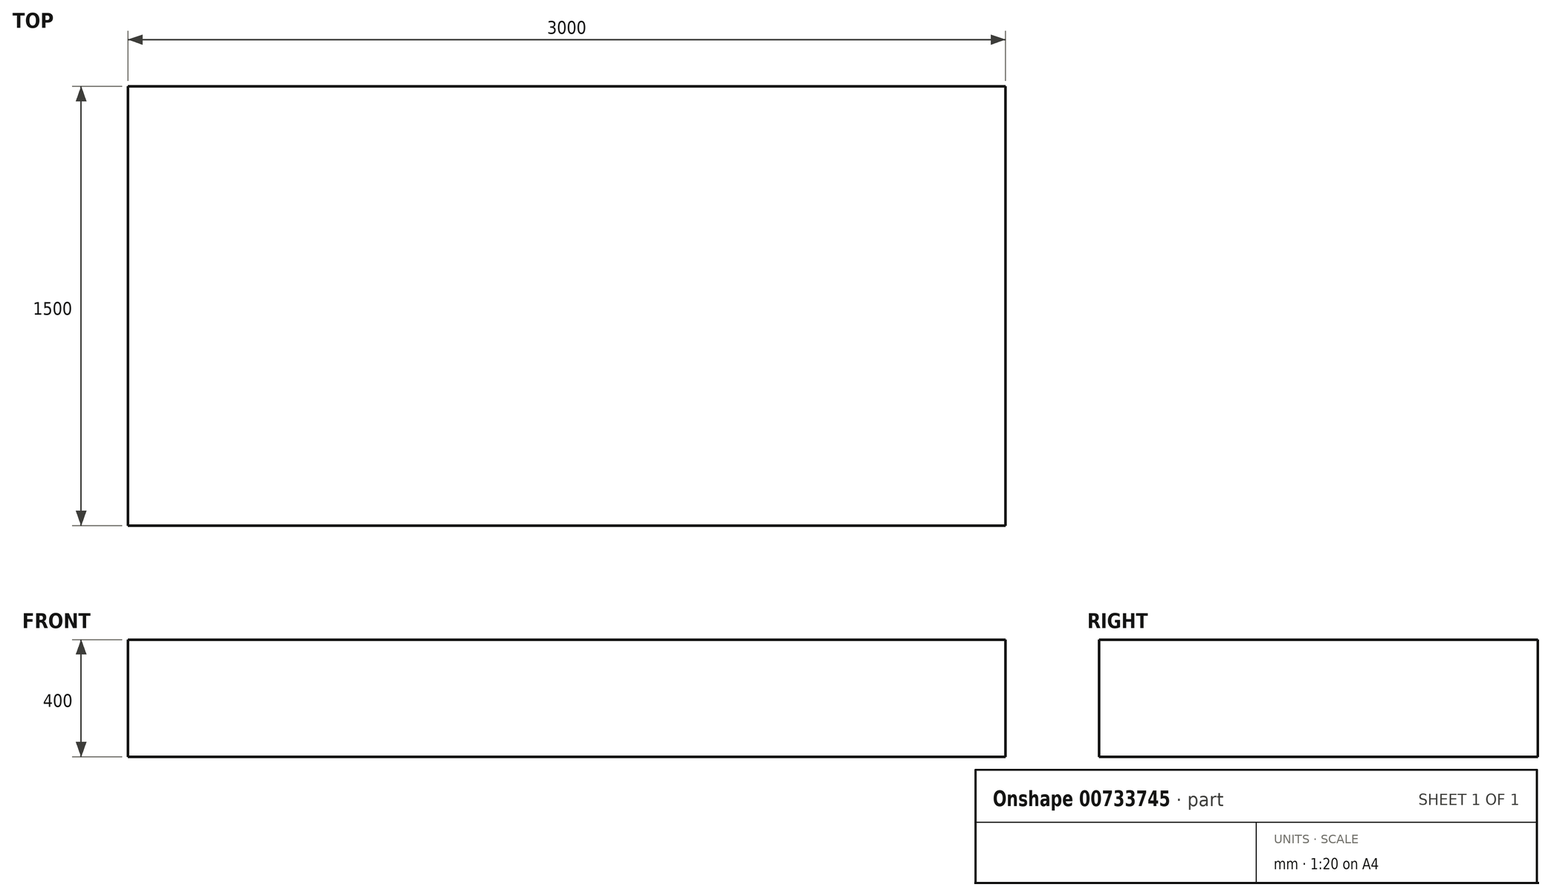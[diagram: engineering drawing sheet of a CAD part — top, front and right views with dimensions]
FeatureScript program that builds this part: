
annotation { "Feature Type Name" : "Feature", "Feature Type Description" : "" }
export const myFeature = defineFeature(function(context is Context, id is Id, definition is map)
    precondition{}
    {
        {
            var Q0;
            Q0=qCreatedBy(makeId("Top.planeOp"),FACE);
            var sketch = newSketch(context, id + "F0", { "sketchPlane" : qUnion([Q0])});
            skLineSegment(sketch, "E0.bottom", {"start": v(1500, -750) * mm, "end": v(-1500, -750) * mm});
            skLineSegment(sketch, "E0.top", {"start": v(1500, 750) * mm, "end": v(-1500, 750) * mm});
            skLineSegment(sketch, "E0.left", {"start": v(1500, -750) * mm, "end": v(1500, 750) * mm});
            skLineSegment(sketch, "E0.right", {"start": v(-1500, -750) * mm, "end": v(-1500, 750) * mm});
            skPoint(sketch, "E0.middle", {"position": v(0, 0) * mm});
            skSolve(sketch);
        }
        {
            var Q0;
            Q0=makeQuery(id+"F0.imprint","IMPRINT",FACE,{"disambiguationData":[TD([[makeQuery(id+"F0.imprint","IMPRINT",EDGE,{"derivedFrom":sQuery(id+"F0.wireOp",EDGE,"E0.bottom")}),-1.0]])]});
            extrude(context, id + "F1", {"entities" : qUnion([Q0]), "depth" : 400 * mm, "offsetDistance" : 25 * mm});
        }
    });
